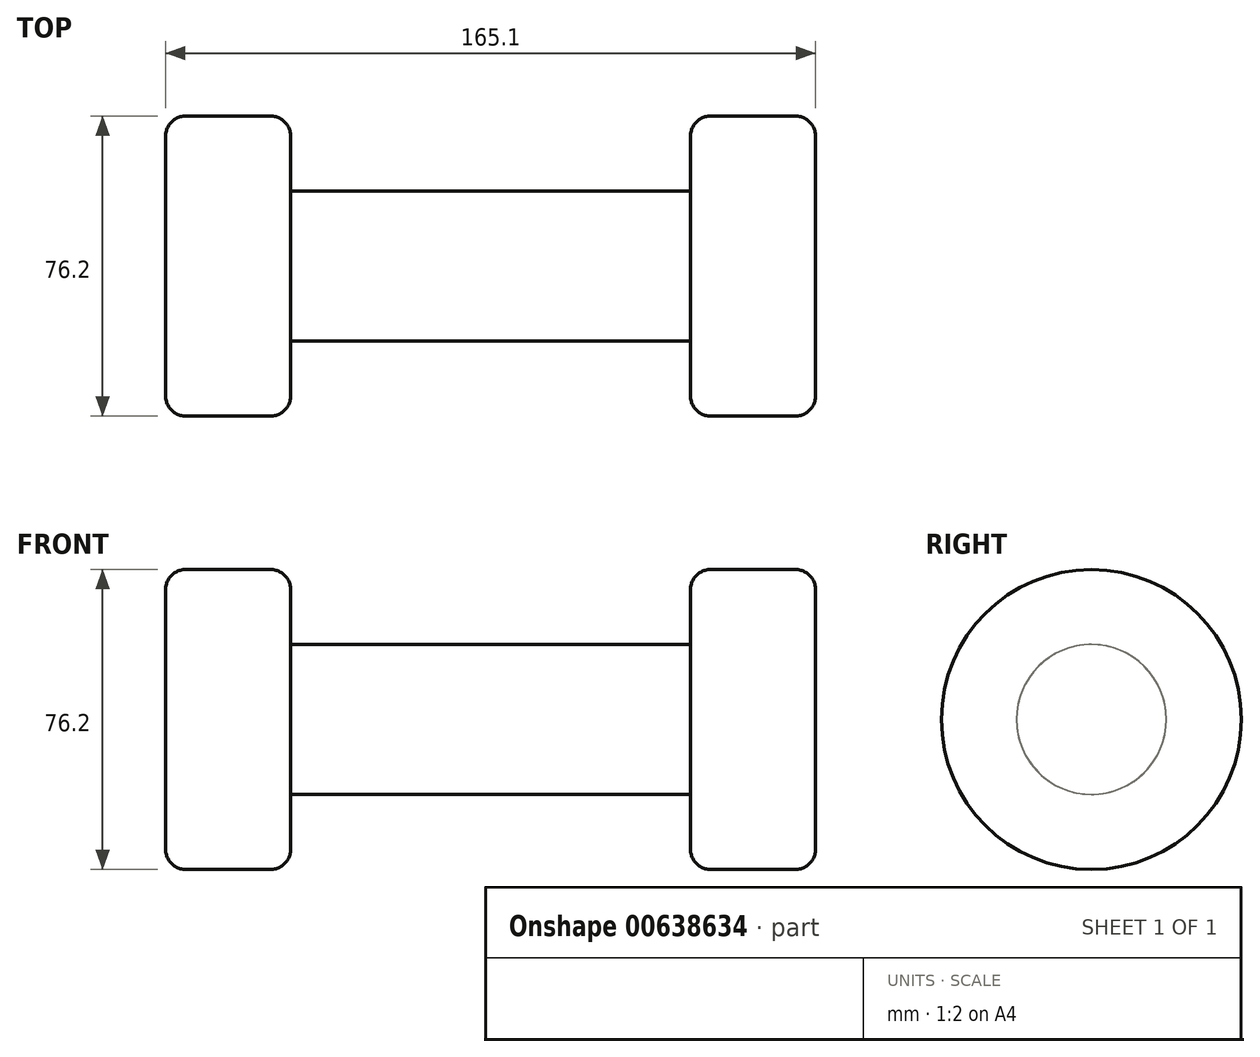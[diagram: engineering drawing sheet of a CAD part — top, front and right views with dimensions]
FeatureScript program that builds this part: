
annotation { "Feature Type Name" : "Feature", "Feature Type Description" : "" }
export const myFeature = defineFeature(function(context is Context, id is Id, definition is map)
    precondition{}
    {
        {
            var Q0;
            Q0=qCreatedBy(makeId("Right.planeOp"),FACE);
            var sketch = newSketch(context, id + "F0", { "sketchPlane" : qUnion([Q0])});
            skCircle(sketch, "E0", {"center": v(0, 0) * mm, "radius": 38.1 * mm});
            skSolve(sketch);
        }
        {
            var Q0;
            Q0 = qSketchRegion(id + "F0", true);
            extrude(context, id + "F1", {"entities" : qUnion([Q0]), "depth" : 31.75 * mm, "offsetDistance" : 25.4 * mm});
        }
        {
            var Q0;
            Q0=makeQuery(id+"F1.opExtrude","CAP_EDGE",EDGE,{"disambiguationData":[OSD([sQuery(id+"F0.wireOp",EDGE,"E0")])],"isStart":true});
            var Q1;
            Q1=makeQuery(id+"F1.opExtrude","CAP_EDGE",EDGE,{"disambiguationData":[OSD([sQuery(id+"F0.wireOp",EDGE,"E0")])],"isStart":false});
            fillet(context, id + "F2", {"entities" : qUnion([Q0, Q1]), "radius" : 5.08 * mm, "tangentPropagation" : true, "allowEdgeOverflow" : false});
        }
        {
            var Q0;
            Q0=makeQuery(id+"F1.opExtrude","CAP_FACE",FACE,{"disambiguationData":[OSD([sQuery(id+"F0.wireOp",EDGE,"E0")])],"isStart":true});
            var sketch = newSketch(context, id + "F3", { "sketchPlane" : qUnion([Q0])});
            skCircle(sketch, "E1", {"center": v(0, 0) * mm, "radius": 19.05 * mm});
            skSolve(sketch);
        }
        {
            var Q0;
            Q0 = qSketchRegion(id + "F3", true);
            extrude(context, id + "F4", {"entities" : qUnion([Q0]), "operationType" : NewBodyOperationType.ADD, "depth" : 101.6 * mm, "offsetDistance" : 25.4 * mm});
        }
        {
            var Q0;
            Q0=makeQuery(id+"F4.opExtrude","CAP_FACE",FACE,{"disambiguationData":[OSD([sQuery(id+"F3.wireOp",EDGE,"E1")])],"isStart":false});
            var sketch = newSketch(context, id + "F5", { "sketchPlane" : qUnion([Q0])});
            skCircle(sketch, "E2", {"center": v(0, 0) * mm, "radius": 38.1 * mm});
            skSolve(sketch);
        }
        {
            var Q0;
            Q0 = qSketchRegion(id + "F5", true);
            extrude(context, id + "F6", {"entities" : qUnion([Q0]), "operationType" : NewBodyOperationType.ADD, "depth" : 31.75 * mm, "offsetDistance" : 25.4 * mm});
        }
        {
            var Q0;
            Q0=makeQuery(id+"F6.opExtrude","CAP_EDGE",EDGE,{"disambiguationData":[OSD([sQuery(id+"F5.wireOp",EDGE,"E2")])],"isStart":true});
            var Q1;
            Q1=makeQuery(id+"F6.opExtrude","CAP_EDGE",EDGE,{"disambiguationData":[OSD([sQuery(id+"F5.wireOp",EDGE,"E2")])],"isStart":false});
            fillet(context, id + "F7", {"entities" : qUnion([Q0, Q1]), "radius" : 5.08 * mm, "tangentPropagation" : true, "allowEdgeOverflow" : false});
        }
    });
